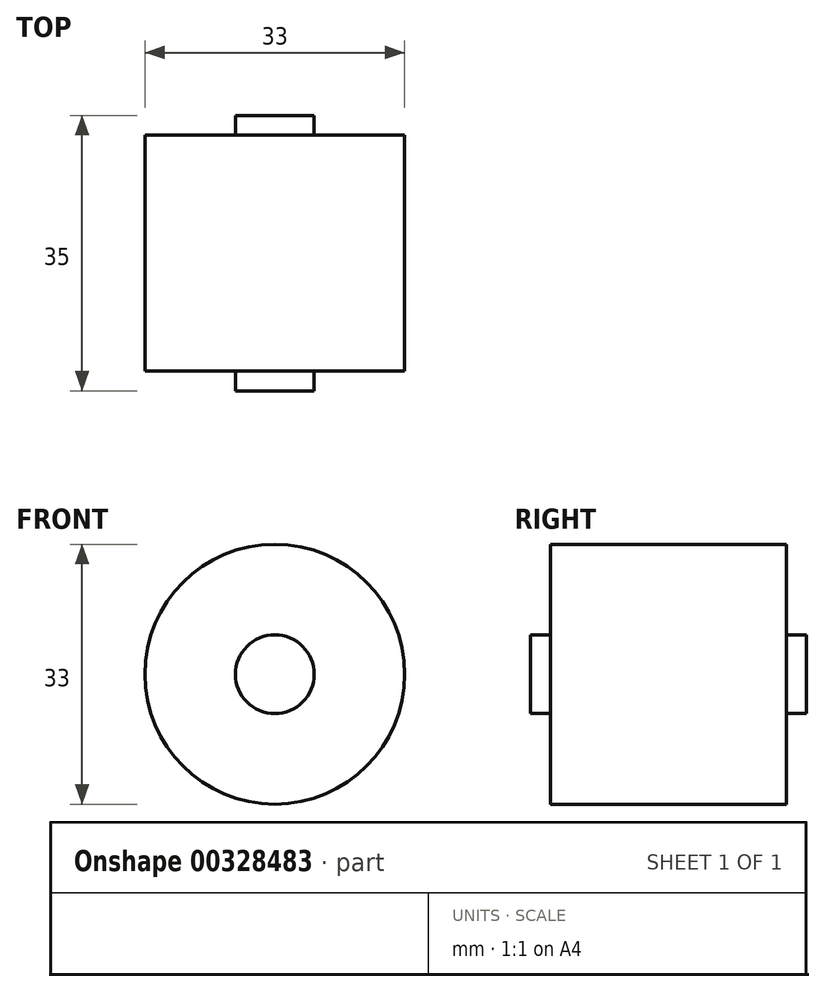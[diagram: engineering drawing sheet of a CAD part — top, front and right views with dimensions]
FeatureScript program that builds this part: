
annotation { "Feature Type Name" : "Feature", "Feature Type Description" : "" }
export const myFeature = defineFeature(function(context is Context, id is Id, definition is map)
    precondition{}
    {
        {
            var Q0;
            Q0=qCreatedBy(makeId("Front.planeOp"),FACE);
            var sketch = newSketch(context, id + "F0", { "sketchPlane" : qUnion([Q0])});
            skCircle(sketch, "E0", {"center": v(-3.57, 0) * mm, "radius": 16.5 * mm});
            skSolve(sketch);
        }
        {
            var Q0;
            Q0=makeQuery(id+"F0.imprint","IMPRINT",FACE,{"disambiguationData":[TD([[makeQuery(id+"F0.imprint","IMPRINT",EDGE,{"derivedFrom":sQuery(id+"F0.wireOp",EDGE,"E0")}),1.0]])]});
            extrude(context, id + "F1", {"entities" : qUnion([Q0]), "depth" : 30 * mm});
        }
        {
            var Q0;
            Q0=makeQuery(id+"F1.opExtrude","CAP_FACE",FACE,{"disambiguationData":[OSD([sQuery(id+"F0.wireOp",EDGE,"E0")])],"isStart":false});
            var sketch = newSketch(context, id + "F2", { "sketchPlane" : qUnion([Q0])});
            skCircle(sketch, "E1", {"center": v(-3.57, 0) * mm, "radius": 5 * mm});
            skSolve(sketch);
        }
        {
            var Q0;
            Q0 = qSketchRegion(id + "F2", true);
            extrude(context, id + "F3", {"entities" : qUnion([Q0]), "operationType" : NewBodyOperationType.ADD, "depth" : 2.5 * mm});
        }
        {
            var Q0;
            Q0=makeQuery(id+"F1.opExtrude","CAP_FACE",FACE,{"disambiguationData":[OSD([sQuery(id+"F0.wireOp",EDGE,"E0")])],"isStart":true});
            var sketch = newSketch(context, id + "F4", { "sketchPlane" : qUnion([Q0])});
            skCircle(sketch, "E2", {"center": v(3.57, 0) * mm, "radius": 5 * mm});
            skSolve(sketch);
        }
        {
            var Q0;
            Q0=makeQuery(id+"F4.imprint","IMPRINT",FACE,{"disambiguationData":[TD([[makeQuery(id+"F4.imprint","IMPRINT",EDGE,{"derivedFrom":sQuery(id+"F4.wireOp",EDGE,"E2")}),1.0]])]});
            extrude(context, id + "F5", {"entities" : qUnion([Q0]), "operationType" : NewBodyOperationType.ADD, "depth" : 2.5 * mm});
        }
    });
